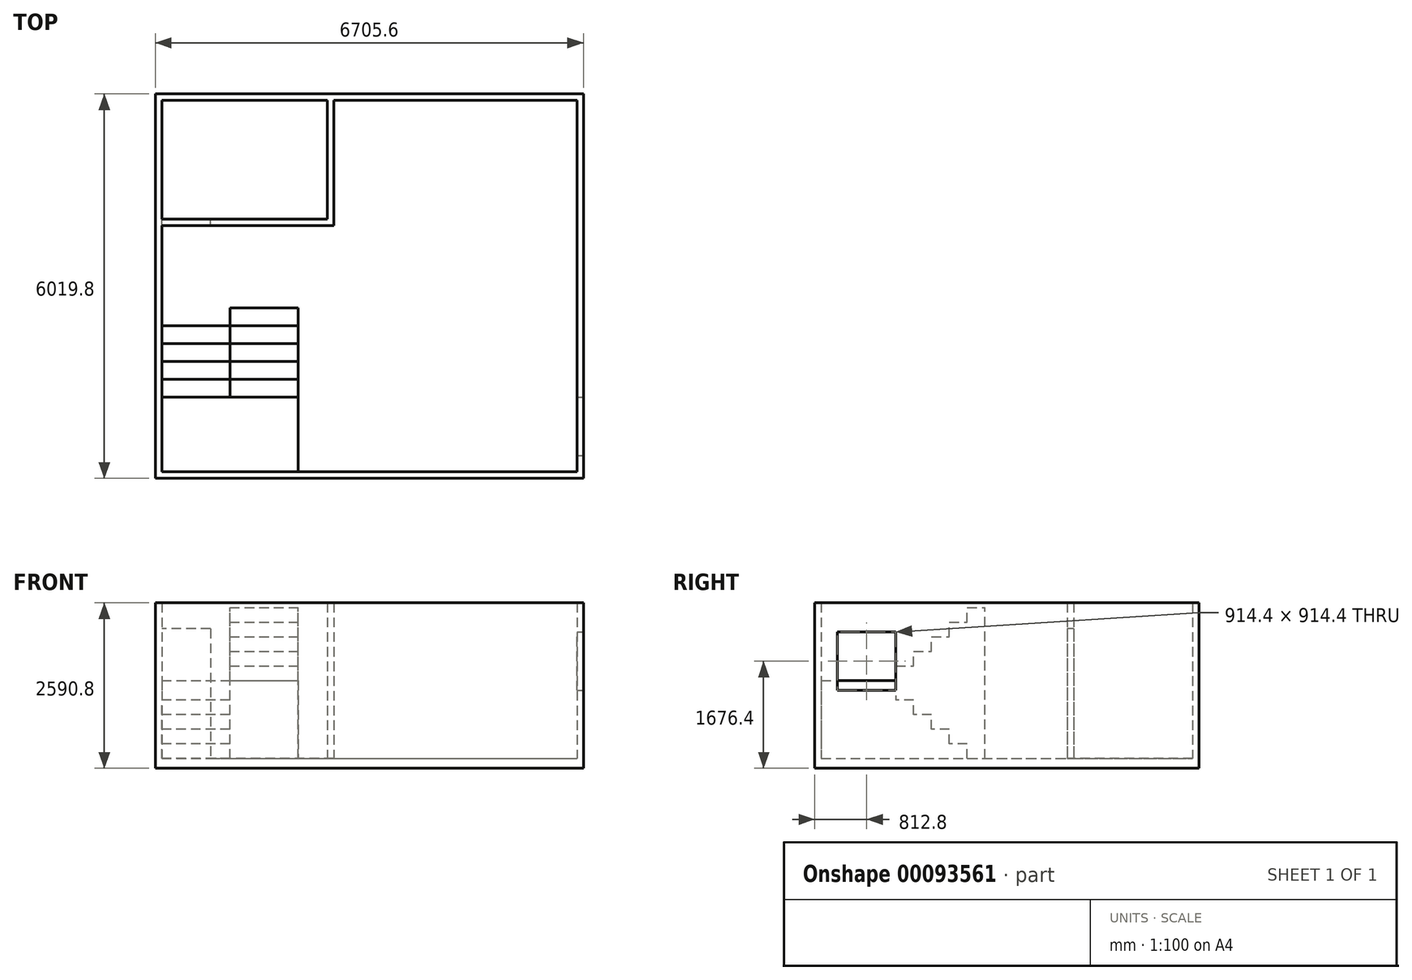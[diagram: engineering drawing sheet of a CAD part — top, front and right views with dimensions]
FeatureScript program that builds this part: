
annotation { "Feature Type Name" : "Feature", "Feature Type Description" : "" }
export const myFeature = defineFeature(function(context is Context, id is Id, definition is map)
    precondition{}
    {
        {
            var Q0;
            Q0=qCreatedBy(makeId("Top.planeOp"),FACE);
            var sketch = newSketch(context, id + "F0", { "sketchPlane" : qUnion([Q0])});
            skLineSegment(sketch, "E0.bottom", {"start": v(0, 0) * mm, "end": v(6705.6, 0) * mm});
            skLineSegment(sketch, "E0.top", {"start": v(0, -6019.8) * mm, "end": v(6705.6, -6019.8) * mm});
            skLineSegment(sketch, "E0.left", {"start": v(0, 0) * mm, "end": v(0, -6019.8) * mm});
            skLineSegment(sketch, "E0.right", {"start": v(6705.6, 0) * mm, "end": v(6705.6, -6019.8) * mm});
            skSolve(sketch);
        }
        {
            var Q0;
            Q0 = qSketchRegion(id + "F0", true);
            extrude(context, id + "F1", {"entities" : qUnion([Q0]), "oppositeDirection" : true, "depth" : 152.4 * mm});
        }
        {
            var Q0;
            Q0=makeQuery(id+"F1.opExtrude","CAP_FACE",FACE,{"disambiguationData":[OSD([sQuery(id+"F0.wireOp",EDGE,"E0.bottom"),sQuery(id+"F0.wireOp",EDGE,"E0.top"),sQuery(id+"F0.wireOp",EDGE,"E0.left"),sQuery(id+"F0.wireOp",EDGE,"E0.right")])],"isStart":true});
            var sketch = newSketch(context, id + "F2", { "sketchPlane" : qUnion([Q0])});
            skLineSegment(sketch, "E1.bottom", {"start": v(0, -6019.8) * mm, "end": v(6705.6, -6019.8) * mm});
            skLineSegment(sketch, "E1.top", {"start": v(0, 0) * mm, "end": v(6705.6, 0) * mm});
            skLineSegment(sketch, "E1.left", {"start": v(0, -6019.8) * mm, "end": v(0, 0) * mm});
            skLineSegment(sketch, "E1.right", {"start": v(6705.6, -6019.8) * mm, "end": v(6705.6, 0) * mm});
            skLineSegment(sketch, "E2.bottom", {"start": v(101.6, -5918.2) * mm, "end": v(6604, -5918.2) * mm});
            skLineSegment(sketch, "E2.top", {"start": v(101.6, -101.6) * mm, "end": v(6604, -101.6) * mm});
            skLineSegment(sketch, "E2.left", {"start": v(101.6, -5918.2) * mm, "end": v(101.6, -101.6) * mm});
            skLineSegment(sketch, "E2.right", {"start": v(6604, -5918.2) * mm, "end": v(6604, -101.6) * mm});
            skSolve(sketch);
        }
        {
            var Q0;
            Q0 = qSketchRegion(id + "F2", true);
            extrude(context, id + "F3", {"entities" : qUnion([Q0]), "operationType" : NewBodyOperationType.ADD, "depth" : 2438.4 * mm});
        }
        {
            var Q0;
            Q0=makeQuery(id+"F1.opExtrude","CAP_FACE",FACE,{"disambiguationData":[OSD([sQuery(id+"F0.wireOp",EDGE,"E0.bottom"),sQuery(id+"F0.wireOp",EDGE,"E0.top"),sQuery(id+"F0.wireOp",EDGE,"E0.left"),sQuery(id+"F0.wireOp",EDGE,"E0.right")])],"isStart":true});
            var sketch = newSketch(context, id + "F4", { "sketchPlane" : qUnion([Q0])});
            skLineSegment(sketch, "E3", {"start": v(863.6, -1962.15) * mm, "end": v(2692.4, -1962.15) * mm});
            skLineSegment(sketch, "E4", {"start": v(2692.4, -1962.15) * mm, "end": v(2692.4, -101.6) * mm});
            skLineSegment(sketch, "E5", {"start": v(2692.4, -101.6) * mm, "end": v(2794, -101.6) * mm});
            skLineSegment(sketch, "E6", {"start": v(2794, -101.6) * mm, "end": v(2794, -2063.75) * mm});
            skLineSegment(sketch, "E7", {"start": v(2794, -2063.75) * mm, "end": v(863.6, -2063.75) * mm});
            skLineSegment(sketch, "E8", {"start": v(863.6, -2063.75) * mm, "end": v(863.6, -1962.15) * mm});
            skSolve(sketch);
        }
        {
            var Q0;
            Q0 = qSketchRegion(id + "F4", true);
            extrude(context, id + "F5", {"entities" : qUnion([Q0]), "operationType" : NewBodyOperationType.ADD, "depth" : 2438.4 * mm});
        }
        {
            var Q0;
            Q0=makeQuery(id+"F3.boolean.opBoolean","MERGE",FACE,{"derivedFrom":[makeQuery(id+"F1.opExtrude","SWEPT_FACE",FACE,{"disambiguationData":[OSD([sQuery(id+"F0.wireOp",EDGE,"E0.right")])]}),makeQuery(id+"F3.opExtrude","SWEPT_FACE",FACE,{"disambiguationData":[OSD([sQuery(id+"F2.wireOp",EDGE,"E1.right")])]})]});
            var sketch = newSketch(context, id + "F6", { "sketchPlane" : qUnion([Q0])});
            skLineSegment(sketch, "E9.bottom", {"start": v(-5664.2, 1981.2) * mm, "end": v(-4749.8, 1981.2) * mm});
            skLineSegment(sketch, "E9.top", {"start": v(-5664.2, 1066.8) * mm, "end": v(-4749.8, 1066.8) * mm});
            skLineSegment(sketch, "E9.left", {"start": v(-5664.2, 1981.2) * mm, "end": v(-5664.2, 1066.8) * mm});
            skLineSegment(sketch, "E9.right", {"start": v(-4749.8, 1981.2) * mm, "end": v(-4749.8, 1066.8) * mm});
            skSolve(sketch);
        }
        {
            var Q0;
            Q0 = qSketchRegion(id + "F6", true);
            extrude(context, id + "F7", {"entities" : qUnion([Q0]), "operationType" : NewBodyOperationType.REMOVE, "oppositeDirection" : true, "depth" : 127 * mm});
        }
        {
            var Q0;
            Q0=makeQuery(id+"F5.opExtrude","SWEPT_FACE",FACE,{"disambiguationData":[OSD([sQuery(id+"F4.wireOp",EDGE,"E7")])]});
            var sketch = newSketch(context, id + "F8", { "sketchPlane" : qUnion([Q0])});
            skLineSegment(sketch, "E10.0", {"start": v(101.6, 2438.4) * mm, "end": v(101.6, 2032) * mm});
            skLineSegment(sketch, "E11", {"start": v(101.6, 2438.4) * mm, "end": v(863.6, 2438.4) * mm});
            skLineSegment(sketch, "E12", {"start": v(863.6, 2438.4) * mm, "end": v(863.6, 2032) * mm});
            skLineSegment(sketch, "E13", {"start": v(863.6, 2032) * mm, "end": v(101.6, 2032) * mm});
            skPoint(sketch, "E14.orphan", {"position": v(101.6, 0) * mm});
            skSolve(sketch);
        }
        {
            var Q0;
            Q0 = qSketchRegion(id + "F8", true);
            var Q1;
            Q1=makeQuery(id+"F5.opExtrude","SWEPT_FACE",FACE,{"disambiguationData":[OSD([sQuery(id+"F4.wireOp",EDGE,"E3")])]});
            extrude(context, id + "F9", {"entities" : qUnion([Q0]), "operationType" : NewBodyOperationType.ADD, "endBound" : BoundingType.UP_TO_SURFACE, "oppositeDirection" : true, "endBoundEntityFace" : qUnion([Q1]), "depth" : 25.4 * mm});
        }
        {
            var Q0;
            Q0=makeQuery(id+"F1.opExtrude","CAP_FACE",FACE,{"disambiguationData":[OSD([sQuery(id+"F0.wireOp",EDGE,"E0.bottom"),sQuery(id+"F0.wireOp",EDGE,"E0.top"),sQuery(id+"F0.wireOp",EDGE,"E0.left"),sQuery(id+"F0.wireOp",EDGE,"E0.right")])],"isStart":true});
            var sketch = newSketch(context, id + "F10", { "sketchPlane" : qUnion([Q0])});
            skLineSegment(sketch, "E15.bottom", {"start": v(101.6, -5918.2) * mm, "end": v(2235.2, -5918.2) * mm});
            skLineSegment(sketch, "E15.top", {"start": v(101.6, -4749.8) * mm, "end": v(2235.2, -4749.8) * mm});
            skLineSegment(sketch, "E15.left", {"start": v(101.6, -5918.2) * mm, "end": v(101.6, -4749.8) * mm});
            skLineSegment(sketch, "E15.right", {"start": v(2235.2, -5918.2) * mm, "end": v(2235.2, -4749.8) * mm});
            skSolve(sketch);
        }
        {
            var Q0;
            Q0 = qSketchRegion(id + "F10", true);
            extrude(context, id + "F11", {"entities" : qUnion([Q0]), "operationType" : NewBodyOperationType.ADD, "depth" : 1219.2 * mm});
        }
        {
            var Q0;
            Q0=makeQuery(id+"F3.opExtrude","SWEPT_FACE",FACE,{"disambiguationData":[OSD([sQuery(id+"F2.wireOp",EDGE,"E2.left")])]});
            var sketch = newSketch(context, id + "F12", { "sketchPlane" : qUnion([Q0])});
            skLineSegment(sketch, "E16", {"start": v(-3632.2, 0) * mm, "end": v(-3632.2, 228.6) * mm});
            skLineSegment(sketch, "E17", {"start": v(-3632.2, 228.6) * mm, "end": v(-3911.6, 228.6) * mm});
            skLineSegment(sketch, "E18", {"start": v(-3911.6, 228.6) * mm, "end": v(-3911.6, 457.2) * mm});
            skLineSegment(sketch, "E19", {"start": v(-3911.6, 457.2) * mm, "end": v(-4191, 457.2) * mm});
            skLineSegment(sketch, "E20", {"start": v(-4191, 457.2) * mm, "end": v(-4191, 685.8) * mm});
            skLineSegment(sketch, "E21", {"start": v(-4191, 685.8) * mm, "end": v(-4470.4, 685.8) * mm});
            skLineSegment(sketch, "E22", {"start": v(-4470.4, 685.8) * mm, "end": v(-4470.4, 914.4) * mm});
            skLineSegment(sketch, "E23", {"start": v(-4470.4, 914.4) * mm, "end": v(-4749.8, 914.4) * mm});
            skLineSegment(sketch, "E24", {"start": v(-4749.8, 914.4) * mm, "end": v(-4749.8, 0) * mm});
            skLineSegment(sketch, "E25", {"start": v(-4749.8, 0) * mm, "end": v(-3632.2, 0) * mm});
            skSolve(sketch);
        }
        {
            var Q0;
            Q0 = qSketchRegion(id + "F12", true);
            extrude(context, id + "F13", {"entities" : qUnion([Q0]), "operationType" : NewBodyOperationType.ADD, "depth" : 1066.8 * mm});
        }
        {
            var Q0;
            Q0=makeQuery(id+"F11.opExtrude","SWEPT_FACE",FACE,{"disambiguationData":[OSD([sQuery(id+"F10.wireOp",EDGE,"E15.right")])]});
            var sketch = newSketch(context, id + "F14", { "sketchPlane" : qUnion([Q0])});
            skLineSegment(sketch, "E26", {"start": v(-4749.8, 1219.2) * mm, "end": v(-4749.8, 1447.8) * mm});
            skLineSegment(sketch, "E27", {"start": v(-4749.8, 1447.8) * mm, "end": v(-4470.4, 1447.8) * mm});
            skLineSegment(sketch, "E28", {"start": v(-4470.4, 1447.8) * mm, "end": v(-4470.4, 1676.4) * mm});
            skLineSegment(sketch, "E29", {"start": v(-4470.4, 1676.4) * mm, "end": v(-4191, 1676.4) * mm});
            skLineSegment(sketch, "E30", {"start": v(-4191, 1676.4) * mm, "end": v(-4191, 1905) * mm});
            skLineSegment(sketch, "E31", {"start": v(-4191, 1905) * mm, "end": v(-3911.6, 1905) * mm});
            skLineSegment(sketch, "E32", {"start": v(-3911.6, 1905) * mm, "end": v(-3911.6, 2133.6) * mm});
            skLineSegment(sketch, "E33", {"start": v(-3911.6, 2133.6) * mm, "end": v(-3632.2, 2133.6) * mm});
            skLineSegment(sketch, "E34", {"start": v(-3632.2, 2133.6) * mm, "end": v(-3632.2, 2362.2) * mm});
            skLineSegment(sketch, "E35", {"start": v(-3632.2, 2362.2) * mm, "end": v(-3352.8, 2362.2) * mm});
            skLineSegment(sketch, "E36.0", {"start": v(-4749.8, 1219.2) * mm, "end": v(-4749.8, 0) * mm});
            skLineSegment(sketch, "E37", {"start": v(-4749.8, 0) * mm, "end": v(-3352.8, 0) * mm});
            skLineSegment(sketch, "E38", {"start": v(-3352.8, 0) * mm, "end": v(-3352.8, 2362.2) * mm});
            skSolve(sketch);
        }
        {
            var Q0;
            Q0 = qSketchRegion(id + "F14", true);
            extrude(context, id + "F15", {"entities" : qUnion([Q0]), "operationType" : NewBodyOperationType.ADD, "oppositeDirection" : true, "depth" : 1066.8 * mm});
        }
    });
